SOLIDWORKS PART (.sldprt)
format: sldprt  version: not decoded by parser v0  size: 438,784 bytes
history: native  units: mm
features: sketch x4, cut_extrude x3, pattern_circular x2, material x1, revolve x1, chamfer x1 (+13 scaffold rows collapsed)
feature tree (25):
  scaffold x13  (default folders/planes/origin — collapsed)
  material  "Chrome Stainless Steel"
  sketch  "Sketch1"  dims[c1.D1=5.715mm c1.D2=10.0mm c1.D3=17.018mm c1.D4=3.556mm c1.D5=10.16mm c1.D6=1.016mm c1.D7=6.35mm c1.D8=6.985mm c1.D9=1.6002mm c1.D10=1.016mm c2.D5=15.24mm c2.D11=3.302mm c2.D6=2.54mm c2.D7=7.366mm]
  revolve  "Revolve1"  Angle=360deg
  sketch  "Sketch2"  dims[D1=1.5875mm]
  cut_extrude  "Cut-Extrude1"  Depth=2.032mm
  sketch  "Sketch3"  dims[c1.D2=15.24mm c1.D1=~7.239356mm c2.D1=9.0deg]
  cut_extrude  "Cut-Extrude2"  [1 undecoded]
  pattern_circular  "CirPattern1"  Count=40 Angle=360deg
  chamfer  "Chamfer1"  Distance=0.254mm Angle=45deg
  sketch  "Sketch4"  dims[c1.D2=5.334mm c1.D1=~1.501838mm c2.D1=~6.238121deg]
  cut_extrude  "Cut-Extrude3"  [1 undecoded]
  pattern_circular  "CirPattern2"  Count=50 Angle=360deg
decode coverage: 9 of 11 modeling features carry decoded parameters
note: ~ marks probable driven/reference dimensions
note: 2 parameter values undecoded
note: suppression state not decoded; provenance and decode notes live in map.json
